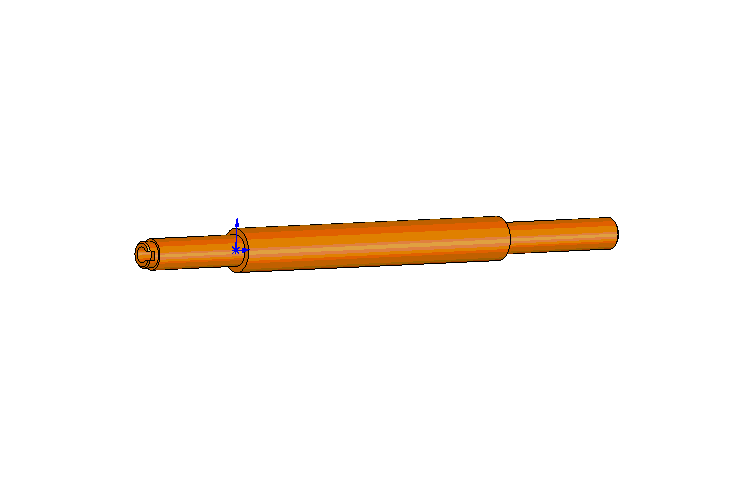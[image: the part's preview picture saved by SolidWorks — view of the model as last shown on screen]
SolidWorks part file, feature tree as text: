
SOLIDWORKS PART (.sldprt)
format: sldprt  version: not decoded by parser v0  size: 169,984 bytes
history: native  units: mm
features: sketch x4, plane x3, extrude x2, cut_extrude x2, material x1, chamfer x1 (+10 scaffold rows collapsed)
feature tree (23):
  scaffold x10  (default folders/planes/origin — collapsed)
  material  "Matériau <non spécifié>"
  plane  "Plan de face"
  plane  "Plan de dessus"
  plane  "Plan de droite"
  sketch  "Esquisse1"  dims[D1=14.0mm]
  extrude  "Extrusion1"  Depth=100mm
  sketch  "Esquisse2"  dims[D1=10.0mm D2=5.0mm]
  extrude  "Extrusion2"  Depth=36mm
  sketch  "Esquisse3"  dims[D1=8.5mm]
  cut_extrude  "Enlèv. mat.-Extru.1"  Depth=3.5mm
  sketch  "Esquisse4"  dims[D1=2.0mm D2=3.0mm]
  cut_extrude  "Enlèv. mat.-Extru.2"  [1 undecoded]
  chamfer  "Chanfrein1"  Distance=0.5mm Angle=45deg
decode coverage: 8 of 9 modeling features carry decoded parameters
note: 1 parameter value undecoded
note: suppression state not decoded; provenance and decode notes live in map.json
